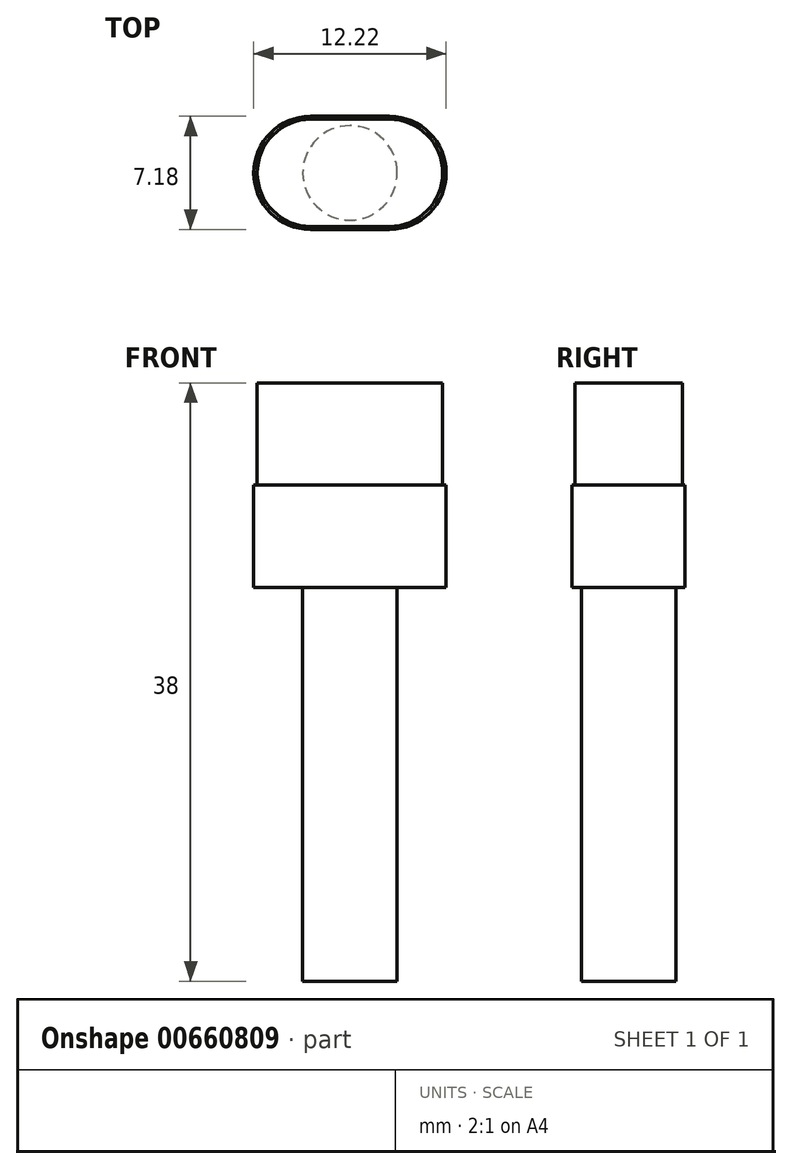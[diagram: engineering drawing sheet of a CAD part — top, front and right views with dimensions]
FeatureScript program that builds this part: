
annotation { "Feature Type Name" : "Feature", "Feature Type Description" : "" }
export const myFeature = defineFeature(function(context is Context, id is Id, definition is map)
    precondition{}
    {
        {
            var Q0;
            Q0=qCreatedBy(makeId("Top.planeOp"),FACE);
            var sketch = newSketch(context, id + "F0", { "sketchPlane" : qUnion([Q0])});
            skArc(sketch, "E0", {"start": v(-2.52, 3.6) * mm, "mid": v(-6.11, 0) * mm, "end": v(-2.52, -3.59) * mm});
            skLineSegment(sketch, "E1", {"start": v(-2.52, 3.6) * mm, "end": v(2.52, 3.6) * mm});
            skLineSegment(sketch, "E2", {"start": v(-2.52, -3.59) * mm, "end": v(2.52, -3.59) * mm});
            skArc(sketch, "E3", {"start": v(2.52, -3.59) * mm, "mid": v(6.11, 0) * mm, "end": v(2.52, 3.6) * mm});
            skPoint(sketch, "E3.centerSnap0", {"position": v(-2.91, 0) * mm});
            skLineSegment(sketch, "E4", {"start": v(-2.52, 0) * mm, "end": v(-6.11, 0) * mm, "construction": true});
            skLineSegment(sketch, "E5", {"start": v(0, 0) * mm, "end": v(6.11, 0) * mm, "construction": true});
            skSolve(sketch);
        }
        {
            var Q0;
            Q0=qSketchRegion(id+"F0",true);
            extrude(context, id + "F1", {"entities" : qUnion([Q0]), "depth" : 6.5 * mm, "offsetDistance" : 25 * mm});
        }
        {
            var Q0;
            Q0=makeQuery(id+"F1.opExtrude","CAP_FACE",FACE,{"disambiguationData":[OSD([sQuery(id+"F0.wireOp",EDGE,"E0"),sQuery(id+"F0.wireOp",EDGE,"E1"),sQuery(id+"F0.wireOp",EDGE,"E2"),sQuery(id+"F0.wireOp",EDGE,"E3")])],"isStart":true});
            var sketch = newSketch(context, id + "F2", { "sketchPlane" : qUnion([Q0])});
            skCircle(sketch, "E6", {"center": v(0, 0) * mm, "radius": 3 * mm});
            skSolve(sketch);
        }
        {
            var Q0;
            Q0=qSketchRegion(id+"F2",true);
            extrude(context, id + "F3", {"entities" : qUnion([Q0]), "operationType" : NewBodyOperationType.ADD, "depth" : 25 * mm, "offsetDistance" : 25 * mm});
        }
        {
            var Q0;
            Q0=makeQuery(id+"F1.opExtrude","CAP_FACE",FACE,{"disambiguationData":[OSD([sQuery(id+"F0.wireOp",EDGE,"E0"),sQuery(id+"F0.wireOp",EDGE,"E1"),sQuery(id+"F0.wireOp",EDGE,"E2"),sQuery(id+"F0.wireOp",EDGE,"E3")])],"isStart":false});
            var sketch = newSketch(context, id + "F4", { "sketchPlane" : qUnion([Q0])});
            skLineSegment(sketch, "E7", {"start": v(0, 0) * mm, "end": v(5.89, 0) * mm});
            skPoint(sketch, "E7.endSnap0", {"position": v(6.11, 0) * mm});
            skLineSegment(sketch, "E8", {"start": v(0, 0) * mm, "end": v(0, 3.4) * mm});
            skPoint(sketch, "E8.endSnap0", {"position": v(0, 3.6) * mm});
            skLineSegment(sketch, "E9", {"start": v(0, 3.4) * mm, "end": v(2.48, 3.4) * mm});
            skLineSegment(sketch, "E10", {"start": v(0, 0) * mm, "end": v(-5.89, 0) * mm});
            skLineSegment(sketch, "E11", {"start": v(-2.48, 3.4) * mm, "end": v(0, 3.4) * mm});
            skLineSegment(sketch, "E12", {"start": v(-2.48, -3.41) * mm, "end": v(0, -3.41) * mm});
            skLineSegment(sketch, "E13", {"start": v(-5.89, 0) * mm, "end": v(-2.48, 0) * mm});
            skLineSegment(sketch, "E14", {"start": v(-2.48, 0) * mm, "end": v(5.89, 0) * mm});
            skLineSegment(sketch, "E15", {"start": v(5.89, 0) * mm, "end": v(2.48, 0) * mm});
            skArc(sketch, "E16", {"start": v(2.48, 3.41) * mm, "mid": v(5.89, 0) * mm, "end": v(2.48, -3.4) * mm});
            skArc(sketch, "E17", {"start": v(-2.48, 3.4) * mm, "mid": v(-5.9, 0) * mm, "end": v(-2.48, -3.41) * mm});
            skPoint(sketch, "E18.end.orphan", {"position": v(-5.95, 3.4) * mm});
            skPoint(sketch, "E19.start.orphan", {"position": v(5.89, -4) * mm});
            skPoint(sketch, "E20.start.orphan", {"position": v(5.89, 3.4) * mm});
            skLineSegment(sketch, "E21", {"start": v(0, 0) * mm, "end": v(0, -3.4) * mm});
            skLineSegment(sketch, "E22", {"start": v(2.48, -3.4) * mm, "end": v(0, -3.41) * mm});
            skSolve(sketch);
        }
        {
            var Q0;
            Q0=qSketchRegion(id+"F4",true);
            extrude(context, id + "F5", {"entities" : qUnion([Q0]), "operationType" : NewBodyOperationType.ADD, "depth" : 6.5 * mm, "offsetDistance" : 25 * mm});
        }
    });
